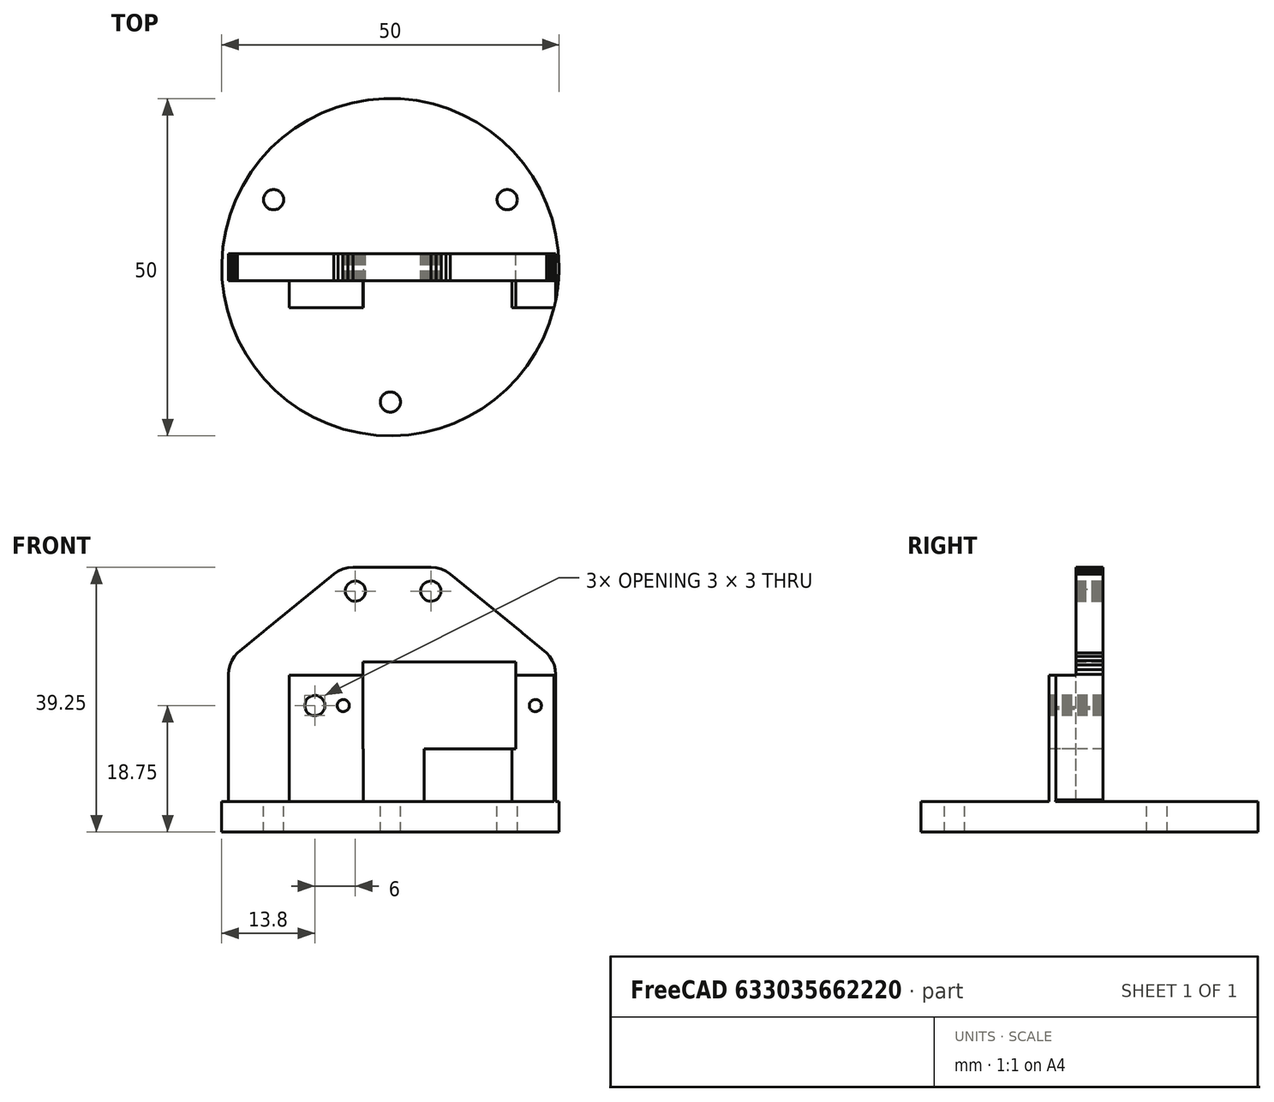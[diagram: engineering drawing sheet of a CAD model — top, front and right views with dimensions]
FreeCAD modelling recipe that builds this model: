
FCSTD DOCUMENT  (FreeCAD 0.16R6078 (Git))
Label: gripper
License: CreativeCommons Attribution-NonCommercial-ShareAlike
LicenseURL: http://creativecommons.org/licenses/by-nc-sa/4.0/
objects: Part::Cylinder×4, Part::MultiFuse×2, Part::FeaturePython×1, Part::Feature×1, Part::MultiCommon×1, Part::Cut×1
note: 10 computed .brp shape members not serialized (recipe doc carries the construction recipe); baked Part::Feature solids carry a one-line shape summary decoded from their .brp

FEATURE [Part::Cylinder] Cylinder621  label="Cylinder1240"
  Angle = 360
  Height = 18
  Placement = pos=(-65,97.5329,30.1) rot=(0,0,1;0rad)
  Radius = 1.5
FEATURE [Part::Cylinder] Cylinder622  label="Cylinder1241"
  Angle = 360
  Height = 6
  Placement = pos=(-65,97.5329,28.1) rot=(0,0,1;0rad)
  Radius = 2.5
FEATURE [Part::MultiFuse] Fusion460
  Placement = pos=(82.3205,-87.5329,579.9) rot=(0,0,1;0rad)
  Shapes = -> [Cylinder621,Cylinder622]
FEATURE [Part::FeaturePython] Array051  # Draft array (typed FeaturePython)
  Angle = 360
  ArrayType = 1
  Axis = (0,0,1)
  Base = -> Fusion460
  Center = (0,0,0)
  Fuse = false
  IntervalAxis = (0,0,0)
  IntervalX = (1,0,0)
  IntervalY = (0,1,0)
  IntervalZ = (0,0,0)
  NumberPolar = 3
  NumberX = 2
  NumberY = 2
  NumberZ = 1
  Placement = pos=(0,0,-622) rot=(0,0,1;0rad)
FEATURE [Part::Cylinder] Cylinder
  Angle = 360
  Height = 4.5
  Placement = pos=(0,0,-0.25) rot=(0,0,1;0rad)
  Radius = 25
FEATURE [Part::Feature] Gripperservoplate_v2001_solid  label="Gripperservoplate_v2001 (Solid)"
  shape: bbox 48.5 x 20 x 39 mm, 2051 faces (baked)
FEATURE [Part::MultiFuse] Fusion
  Shapes = -> [Cylinder,Gripperservoplate_v2001_solid]
FEATURE [Part::Cylinder] Cylinder623
  Angle = 360
  Height = 42.5
  Placement = pos=(0,0,-0.25) rot=(0,0,1;0rad)
  Radius = 25
FEATURE [Part::MultiCommon] Common
  Shapes = -> [Cylinder623,Fusion]
FEATURE [Part::Cut] Cut
  Base = -> Common
  Tool = -> Array051
